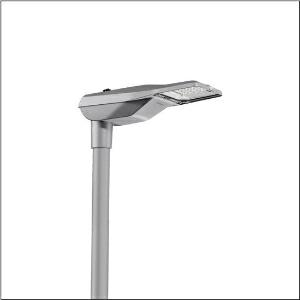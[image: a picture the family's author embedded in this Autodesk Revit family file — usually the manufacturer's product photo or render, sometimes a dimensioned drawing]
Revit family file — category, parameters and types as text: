
# Revit family: streetlight_sl_21_micro___st0_8a_5xe1c43s08db_42f9
name_source: partatom
category: Lighting Fixtures
units: mm (PartAtom-declared; Revit-internal decimal feet)

## family parameters
Cut with Voids When Loaded = No
Host = Face
Light Source = No
Part Type = Normal
Room Calculation Point = No
Round Connector Dimension = Use Diameter
Shared = No

## types (1)
- --- (1 x LED, 5320 lm, 39.1 W, 4000K)
    Apparent Load = 39 VA
    CIE Flux Codes = 38 75 97 100 100
    Color Rendering = 70
    Color Temperature = 4000K
    Default Elevation = 1800 mm
    Description = Streetlight SL 21 micro, mast luminaire, primary light control with lens, of PMMA, primary optical cover: cover, of toughened safety glass, transparent, light distribution: ST0.8a, light emission: direct distribution, primary light characteristic: asymmetric, installation type: side-entry, post-top, LED, High Power LED, rated luminous flux: 5.320lm, luminous efficacy: 136lm/W, light colour: 740, colour temperature: 4000K, control: flexible luminous flux parameterisation, time-dependent luminous flux control, constant luminous flux control, overheat protection, pre-setting: logarithmic dimming characteristic, mains connection: 220..240V, AC, 50/60Hz, start of lifetime: 39W, end of service life: 41W, reduction: 18W, luminaire housing, of diecast aluminium, powder-coated, Siteco® metallic grey (DB 702S), corrosivity category C5 mid according to DIN EN ISO 12944, please order mast flange separately, inclination adjustable: 0°, 5°, 10°, 15°, sealing non-destructively replaceable, multi-level sealing system, length: 528mm, width: 235mm, height: 110mm, mast flange for spigot size: 42mm (side-entry): 5XC10008XM4, 60/48mm (side-entry/post-top): 5XC10108XM2, 76/60mm (side-entry/post-top): 5XC10108XM1, Smart Interface above, protection rating (complete): IP66, insulation class (complete): insulation class II (safety insulation), certification: CE, ENEC, ENEC+, VDE, impact resistance: IK09, permissible operating ambient temperature for outdoor applications: -40..+50°C, standard-compliant lighting for roads and squares, packaging unit: 1 piece

Light Distribution: ST0.8a
    Height = 110 mm
    Lamp = 1 x LED
    Lamp Light Flux = 5320 lm
    Lamp Power = 39.1 W
    Lamp count = 1
    Length = 528 mm
    Luminous efficacy = 136 lm/W
    Manufacturer = Siteco
    ModVariant = No
    Model = 5XE1C43S08DB
    Number of Poles = 1
    OnlyDefault = Yes
    Power Factor = 1
    Product Name = Streetlight SL 21 micro | ST0.8a
    Product group = mast luminaire | pylon top
    ProductGroupID = 6100
    Protection Class = Protection class II
    Protection Degree = IP 66
    RLX_Detail_Level = 1
    RLX_Emergency_Light_Flux = 0 lm
    RLX_Emergency_Type = 0
    RLX_Emergency_Type_DB = No
    RlxData = <blob elided: 98669 chars, md5=c49e7d19>
    Socket = socket
    Standby Power = 0 W
    System Light Flux = 5320 lm
    System Power = 39 W
    Type Comments = factory setting: luminous flux: 100 % | dim-lin: 254 | 765 mA
    Type Image = l_1277292.jpg
    URL = http://relux.com
    VarID = @adj_124761
    Voltage = 0 V
    Weight = 0.00 kg
    Width = 235 mm

## geometry (parser evidence)
native form markers: Blend x4, Sweep x11
no freeform markers — native parametric forms only
